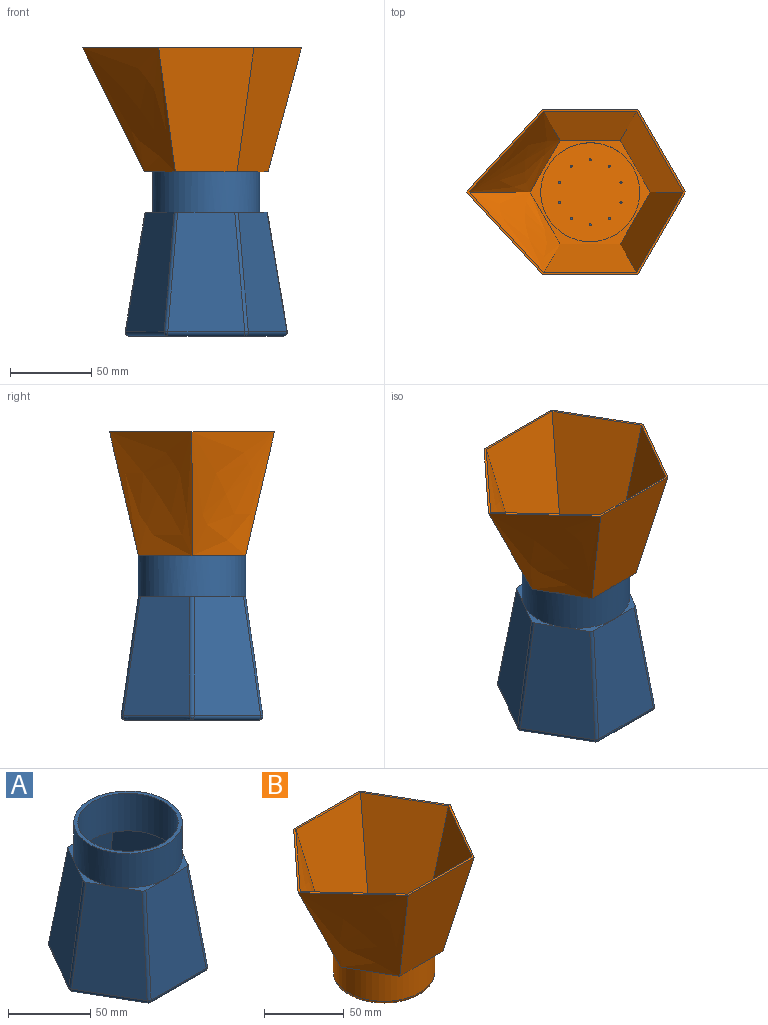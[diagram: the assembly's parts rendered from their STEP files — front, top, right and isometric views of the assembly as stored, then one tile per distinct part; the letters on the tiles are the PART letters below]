
ASSEMBLY  parts=2 mates=1
PART A: 41 faces, bbox 123.6x107.3x313.7 mm
  f0: bspline ~76.2x43.99mm, area 3057.7mm2, adj f4,f5,f12,f14,f15,f31
  f1: bspline ~76.2x43.99mm, area 3057.7mm2, adj f5,f6,f20,f26,f29,f31
  f2: plane 26.78x15.51mm, normal (0,0,1), area 57.4mm2, adj f8,f9,f23,f31
  f3: plane 26.78x15.51mm, normal (0,0,1), area 57.4mm2, adj f7,f8,f17,f31
  f4: plane 31.22x8.78mm, normal (0,0,1), area 57.5mm2, adj f0,f7,f12,f31
  f5: plane 56.41x15.89mm, normal (0,0,1), area 117.2mm2, adj f0,f1,f11,f14,f20,f31
  f6: plane 31.22x8.78mm, normal (0,0,1), area 57.5mm2, adj f1,f9,f29,f31
  f7: plane 73.64x41.4mm, normal (-0.86,-0.49,0.14), area 3058.7mm2, adj f3,f4,f12,f16,f17,f31
  f8: plane 73.64x47.75mm, normal (0,-0.99,0.14), area 3058.6mm2, adj f2,f3,f17,f22,f23,f31
  f9: plane 73.64x41.4mm, normal (0.86,-0.49,0.14), area 3058.7mm2, adj f2,f6,f23,f27,f29,f31
  f10: plane 94.83x82.12mm, normal (0,0,-1), area 5840.7mm2, adj f15,f16,f21,f22,f26,f27
  f11: plane 73.3x47.41mm, normal (0,0.99,0.14), area 3058.6mm2, adj f5,f14,f20,f21
  f12: bspline ~91.99x16.02mm, area 195.4mm2, adj f0,f4,f7,f13
  f13: sphere r=2.54mm, area 13.4mm2, adj f12,f15,f16
  f14: bspline ~91.99x14.46mm, area 195.5mm2, adj f0,f5,f11,f18
  f15: bspline ~58.29x35.35mm, area 206.4mm2, adj f0,f10,f13,f18
  f16: cylinder r=2.54mm len=42.33mm, axis (0.5,-0.87,0), area 206.4mm2, adj f7,f10,f13,f19
  f17: cylinder r=2.54mm len=73.35mm, axis (0.08,0.14,0.99), area 195.4mm2, adj f3,f7,f8,f19
  f18: sphere r=2.54mm, area 7.7mm2, adj f14,f15,f21
  f19: sphere r=2.54mm, area 7.7mm2, adj f16,f17,f22
  f20: bspline ~91.99x14.46mm, area 195.5mm2, adj f1,f5,f11,f24
  f21: cylinder r=2.54mm len=47.41mm, axis (-1,0,0), area 206.4mm2, adj f10,f11,f18,f24
  f22: cylinder r=2.54mm len=47.41mm, axis (1,0,0), area 206.4mm2, adj f8,f10,f19,f25
  f23: cylinder r=2.54mm len=73.35mm, axis (-0.08,0.14,0.99), area 195.4mm2, adj f2,f8,f9,f25
  f24: sphere r=2.54mm, area 9.1mm2, adj f20,f21,f26
  f25: sphere r=2.54mm, area 7.7mm2, adj f22,f23,f27
  f26: bspline ~58.29x35.35mm, area 206.4mm2, adj f1,f10,f24,f28
  f27: cylinder r=2.54mm len=42.33mm, axis (0.5,0.87,0), area 206.4mm2, adj f9,f10,f25,f28
  f28: sphere r=2.54mm, area 10.7mm2, adj f26,f27,f29
  f29: bspline ~91.99x16.02mm, area 195.4mm2, adj f1,f6,f9,f28
  f30: plane 66.04x66.04mm, normal (0,0,1), area 506.7mm2, adj f31,f40
  f31: cylinder r=33.02mm len=66.04mm, axis (0,0,1), area 5269.8mm2, adj f0,f1,f2,f3,f4,f5,f6,f7
  f32: offset ~309.88x78.4mm, area 2980.1mm2, adj f34,f35,f38,f39
  f33: offset ~309.88x78.4mm, area 2980.1mm2, adj f34,f37,f38,f39
  f34: plane 71.12x61.64mm, normal (0,0,-1), area 369.2mm2, adj f32,f33,f35,f36,f37,f39,f40
  f35: plane 71.17x41.11mm, normal (0.86,0.49,-0.14), area 2981.1mm2, adj f32,f34,f36,f38
  f36: plane 71.12x47.41mm, normal (0,0.99,-0.14), area 2981.1mm2, adj f34,f35,f37,f38
  f37: plane 71.17x41.11mm, normal (-0.86,0.49,-0.14), area 2981.1mm2, adj f33,f34,f36,f38
  f38: plane 94.83x82.12mm, normal (0,0,1), area 5840.7mm2, adj f32,f33,f35,f36,f37,f39
  f39: plane 71.17x47.47mm, normal (0,-0.99,-0.14), area 2980.8mm2, adj f32,f33,f34,f38
  f40: cylinder r=30.48mm len=60.96mm, axis (0,0,1), area 5350.8mm2, adj f30,f34
PART B: 30 faces, bbox 137.4x104.1x104.1 mm
  f0: cylinder r=31.75mm len=63.5mm, axis (0,0,-1), area 4560.4mm2, adj f2,f29
  f1: plane 58.42x58.42mm, normal (0,0,-1), area 2667.8mm2, adj f19,f20,f21,f22,f23,f24,f25,f26
  f2: plane 76.26x66.04mm, normal (0,0,-1), area 610.1mm2, adj f0,f4,f5,f6,f7,f8,f9
  f3: plane 134.88x101.62mm, normal (0,0,1), area 483.9mm2, adj f4,f5,f6,f7,f8,f9,f13,f14
  f4: plane 76.2x58.66mm, normal (0,0.97,-0.23), area 3786.6mm2, adj f2,f3,f5,f9
  f5: bspline ~76.2x57.14mm, area 4278.1mm2, adj f2,f3,f4,f6
  f6: bspline ~76.2x57.14mm, area 4278.1mm2, adj f2,f3,f5,f7
  f7: plane 76.2x58.66mm, normal (0,-0.97,-0.23), area 3786.6mm2, adj f2,f3,f6,f8
  f8: plane 76.2x50.8mm, normal (0.84,-0.49,-0.23), area 3786.6mm2, adj f2,f3,f7,f9
  f9: plane 76.2x50.8mm, normal (0.84,0.49,-0.23), area 3786.6mm2, adj f2,f3,f4,f8
  f10: cylinder r=30.48mm len=60.96mm, axis (0,0,-1), area 4864.4mm2, adj f11,f12
  f11: plane 60.96x60.96mm, normal (0,0,1), area 2906mm2, adj f10,f19,f20,f21,f22,f23,f24,f25
  f12: plane 74.17x64.06mm, normal (0,0,1), area 638mm2, adj f10,f13,f14,f15,f16,f17,f18
  f13: plane 74.93x57.32mm, normal (0,-0.97,0.23), area 3628.9mm2, adj f3,f12,f14,f18
  f14: offset ~78.74x59.68mm, area 4094.3mm2, adj f3,f12,f13,f15
  f15: offset ~78.74x59.68mm, area 4094.3mm2, adj f3,f12,f14,f16
  f16: plane 74.93x57.32mm, normal (0,0.97,0.23), area 3628.9mm2, adj f3,f12,f15,f17
  f17: plane 74.93x49.5mm, normal (-0.84,0.49,0.23), area 3620.8mm2, adj f3,f12,f16,f18
  f18: plane 74.93x49.5mm, normal (-0.84,-0.49,0.23), area 3620.8mm2, adj f3,f12,f13,f17
  f19: cylinder r=0.64mm len=1.27mm, axis (0,0,-1), area 5.1mm2, adj f1,f11
  f20: cylinder r=0.64mm len=1.27mm, axis (0,0,-1), area 5.1mm2, adj f1,f11
  f21: cylinder r=0.64mm len=1.27mm, axis (0,0,-1), area 5.1mm2, adj f1,f11
  f22: cylinder r=0.64mm len=1.27mm, axis (0,0,-1), area 5.1mm2, adj f1,f11
  f23: cylinder r=0.64mm len=1.27mm, axis (0,0,-1), area 5.1mm2, adj f1,f11
  f24: cylinder r=0.64mm len=1.27mm, axis (0,0,-1), area 5.1mm2, adj f1,f11
  f25: cylinder r=0.64mm len=1.27mm, axis (0,0,-1), area 5.1mm2, adj f1,f11
  f26: cylinder r=0.64mm len=1.27mm, axis (0,0,-1), area 5.1mm2, adj f1,f11
  f27: cylinder r=0.64mm len=1.27mm, axis (0,0,-1), area 5.1mm2, adj f1,f11
  f28: cylinder r=0.64mm len=1.27mm, axis (0,0,-1), area 5.1mm2, adj f1,f11
  f29: torus R=29.21mm, axis (0,0,1), area 772.8mm2, adj f0,f1
PLACE A t=(-19.21,-3.03,-38.7)mm
PLACE B t=(-19.21,-3.03,37.18)mm
MATE fastened B.f0 <-> A.f31  axis (0,0,-1) through (-19.21,-3.03,37.18)mm
